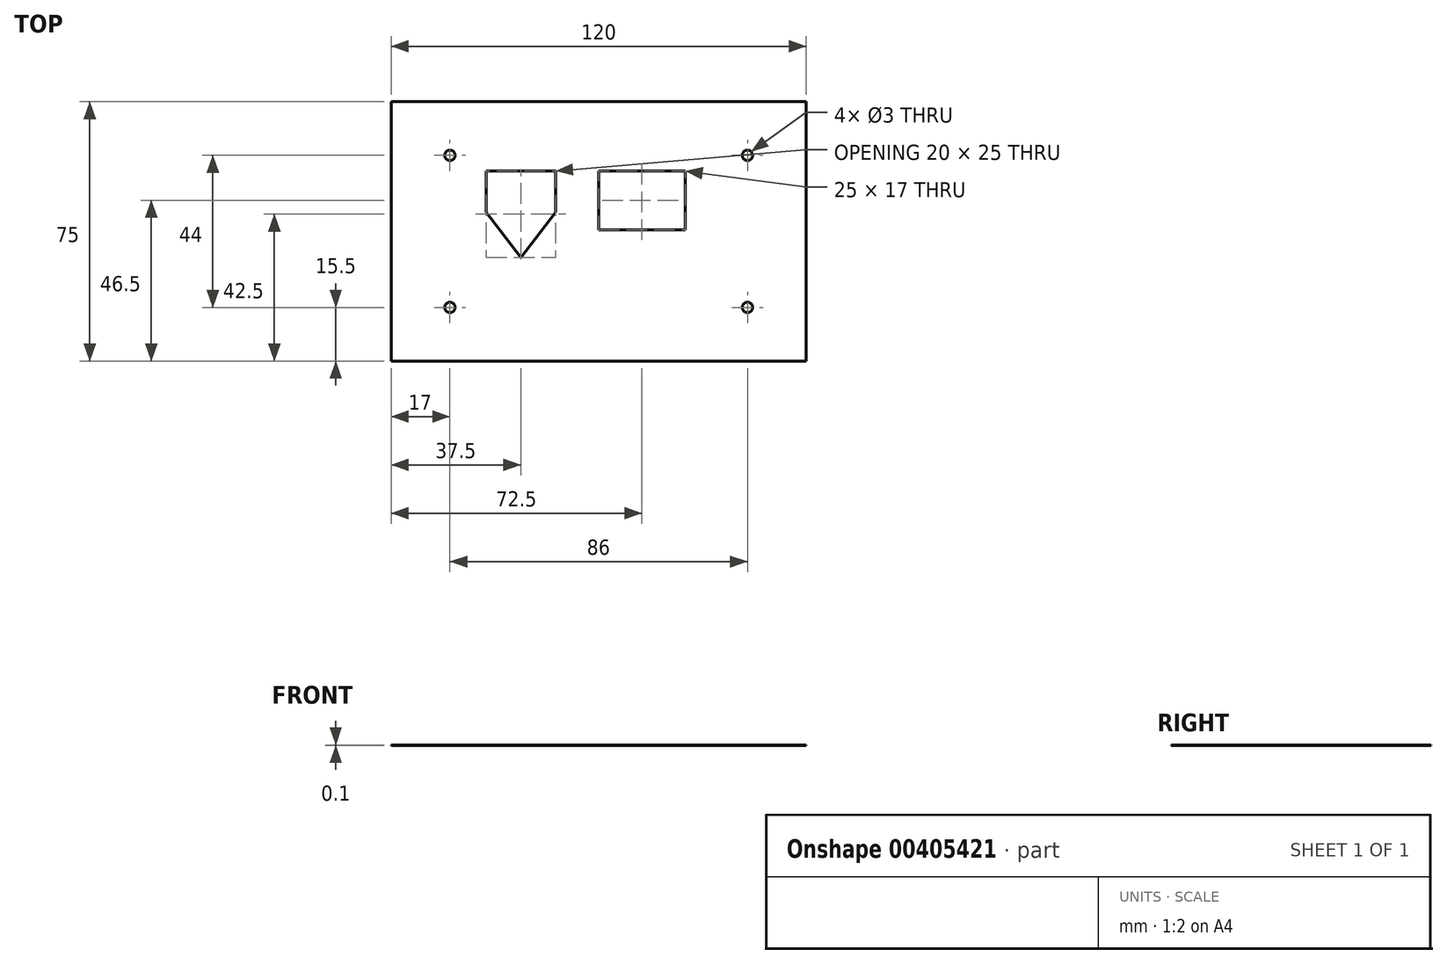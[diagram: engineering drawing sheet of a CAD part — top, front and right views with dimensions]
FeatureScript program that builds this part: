
annotation { "Feature Type Name" : "Feature", "Feature Type Description" : "" }
export const myFeature = defineFeature(function(context is Context, id is Id, definition is map)
    precondition{}
    {
        {
            var Q0;
            Q0=qCreatedBy(makeId("Top.planeOp"),FACE);
            var sketch = newSketch(context, id + "F0", { "sketchPlane" : qUnion([Q0])});
            skLineSegment(sketch, "E0.bottom", {"start": v(60, 37.5) * mm, "end": v(-60, 37.5) * mm});
            skLineSegment(sketch, "E0.top", {"start": v(60, -37.5) * mm, "end": v(-60, -37.5) * mm});
            skLineSegment(sketch, "E0.left", {"start": v(60, 37.5) * mm, "end": v(60, -37.5) * mm});
            skLineSegment(sketch, "E0.right", {"start": v(-60, 37.5) * mm, "end": v(-60, -37.5) * mm});
            skPoint(sketch, "E0.middle", {"position": v(0, 0) * mm});
            skLineSegment(sketch, "E1.bottom", {"start": v(-43, 22) * mm, "end": v(43, 22) * mm, "construction": true});
            skLineSegment(sketch, "E1.top", {"start": v(-43, -22) * mm, "end": v(43, -22) * mm, "construction": true});
            skLineSegment(sketch, "E1.left", {"start": v(-43, 22) * mm, "end": v(-43, -22) * mm, "construction": true});
            skLineSegment(sketch, "E1.right", {"start": v(43, 22) * mm, "end": v(43, -22) * mm, "construction": true});
            skPoint(sketch, "E2.start.orphan", {"position": v(-22.5, 5.5) * mm});
            skCircle(sketch, "E3", {"center": v(-43, 22) * mm, "radius": 1.5 * mm});
            skCircle(sketch, "E4", {"center": v(43, 22) * mm, "radius": 1.5 * mm});
            skCircle(sketch, "E5", {"center": v(43, -22) * mm, "radius": 1.5 * mm});
            skCircle(sketch, "E6", {"center": v(-43, -22) * mm, "radius": 1.5 * mm});
            skPoint(sketch, "E7.left.start.orphan", {"position": v(0, 0.5) * mm});
            skLineSegment(sketch, "E8.top", {"start": v(-12.5, 17.5) * mm, "end": v(-32.5, 17.5) * mm});
            skLineSegment(sketch, "E8.left", {"start": v(-12.5, 5.5) * mm, "end": v(-12.5, 17.5) * mm});
            skLineSegment(sketch, "E8.right", {"start": v(-32.5, 5.5) * mm, "end": v(-32.5, 17.5) * mm});
            skPoint(sketch, "E8.middle", {"position": v(-22.5, 11.5) * mm});
            skLineSegment(sketch, "E9", {"start": v(-12.5, 5.5) * mm, "end": v(-22.5, -7.5) * mm});
            skLineSegment(sketch, "E10", {"start": v(-22.5, -7.5) * mm, "end": v(-32.5, 5.5) * mm});
            skLineSegment(sketch, "E11.bottom", {"start": v(0, 0.5) * mm, "end": v(25, 0.5) * mm});
            skLineSegment(sketch, "E11.top", {"start": v(0, 17.5) * mm, "end": v(25, 17.5) * mm});
            skLineSegment(sketch, "E11.left", {"start": v(0, 0.5) * mm, "end": v(0, 17.5) * mm});
            skLineSegment(sketch, "E11.right", {"start": v(25, 0.5) * mm, "end": v(25, 17.5) * mm});
            skPoint(sketch, "E11.middle", {"position": v(12.5, 9) * mm});
            skSolve(sketch);
        }
        {
            var Q0;
            Q0=makeQuery(id+"F0.imprint","IMPRINT",FACE,{"disambiguationData":[TD([[makeQuery(id+"F0.imprint","IMPRINT",EDGE,{"derivedFrom":sQuery(id+"F0.wireOp",EDGE,"E0.bottom")}),1.0]])]});
            extrude(context, id + "F1", {"entities" : qUnion([Q0]), "depth" : 0.1 * mm});
        }
    });
